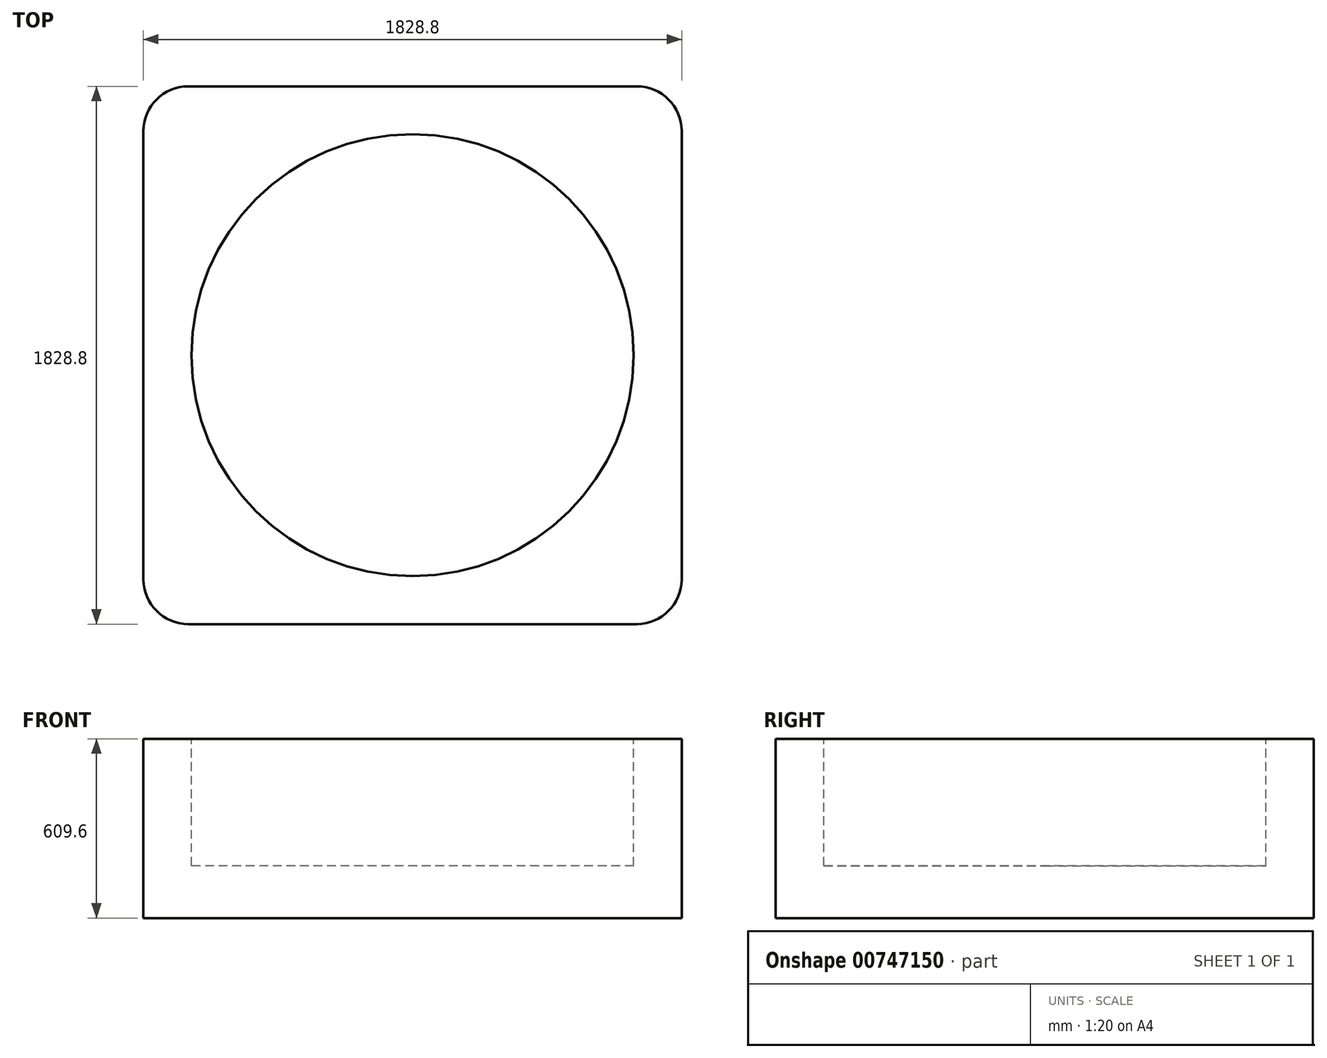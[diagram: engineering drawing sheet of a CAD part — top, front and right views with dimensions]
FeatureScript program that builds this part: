
annotation { "Feature Type Name" : "Feature", "Feature Type Description" : "" }
export const myFeature = defineFeature(function(context is Context, id is Id, definition is map)
    precondition{}
    {
        {
            var Q0;
            Q0=qCreatedBy(makeId("Top.planeOp"),FACE);
            var sketch = newSketch(context, id + "F0", { "sketchPlane" : qUnion([Q0])});
            skLineSegment(sketch, "E0.bottom", {"start": v(-993.4, 881.62) * mm, "end": v(835.4, 881.62) * mm});
            skLineSegment(sketch, "E0.top", {"start": v(-993.4, -947.18) * mm, "end": v(835.4, -947.18) * mm});
            skLineSegment(sketch, "E0.left", {"start": v(-993.4, 881.62) * mm, "end": v(-993.4, -947.18) * mm});
            skLineSegment(sketch, "E0.right", {"start": v(835.4, 881.62) * mm, "end": v(835.4, -947.18) * mm});
            skSolve(sketch);
        }
        {
            var Q0;
            Q0 = qSketchRegion(id + "F0", true);
            extrude(context, id + "F1", {"entities" : qUnion([Q0]), "depth" : 609.6 * mm, "offsetDistance" : 25.4 * mm});
        }
        {
            var Q0;
            Q0=makeQuery(id+"F1.opExtrude","CAP_FACE",FACE,{"disambiguationData":[OSD([sQuery(id+"F0.wireOp",EDGE,"E0.bottom"),sQuery(id+"F0.wireOp",EDGE,"E0.top"),sQuery(id+"F0.wireOp",EDGE,"E0.left"),sQuery(id+"F0.wireOp",EDGE,"E0.right")])],"isStart":false});
            var sketch = newSketch(context, id + "F2", { "sketchPlane" : qUnion([Q0])});
            skCircle(sketch, "E1", {"center": v(-79, -32.78) * mm, "radius": 751.4 * mm});
            skSolve(sketch);
        }
        {
            var Q0;
            Q0 = qSketchRegion(id + "F2", true);
            extrude(context, id + "F3", {"entities" : qUnion([Q0]), "operationType" : NewBodyOperationType.REMOVE, "oppositeDirection" : true, "depth" : 431.8 * mm, "offsetDistance" : 25.4 * mm});
        }
        {
            var Q0;
            Q0=makeQuery(id+"F1.opExtrude","SWEPT_EDGE",EDGE,{"disambiguationData":[OSD([sQuery(id+"F0.wireOp",EDGE,"E0.top"),sQuery(id+"F0.wireOp",EDGE,"E0.left")])]});
            var Q1;
            Q1=makeQuery(id+"F1.opExtrude","SWEPT_EDGE",EDGE,{"disambiguationData":[OSD([sQuery(id+"F0.wireOp",EDGE,"E0.top"),sQuery(id+"F0.wireOp",EDGE,"E0.right")])]});
            var Q2;
            Q2=makeQuery(id+"F1.opExtrude","SWEPT_EDGE",EDGE,{"disambiguationData":[OSD([sQuery(id+"F0.wireOp",EDGE,"E0.bottom"),sQuery(id+"F0.wireOp",EDGE,"E0.right")])]});
            var Q3;
            Q3=makeQuery(id+"F1.opExtrude","SWEPT_EDGE",EDGE,{"disambiguationData":[OSD([sQuery(id+"F0.wireOp",EDGE,"E0.bottom"),sQuery(id+"F0.wireOp",EDGE,"E0.left")])]});
            fillet(context, id + "F4", {"entities" : qUnion([Q0, Q1, Q2, Q3]), "radius" : 152.4 * mm, "tangentPropagation" : true, "allowEdgeOverflow" : false});
        }
    });
